# Revit family: Flachrundschraube mit Kombimutter
name_source: partatom
category: Generic Models
revit_build: Autodesk Revit 2015 (Build: 20140606_1530(x64)
units: mm (PartAtom-declared; Revit-internal decimal feet)

## types (14) — shared parameters
Manufacturer = OBO Bettermann
URL = http://www.obo-bettermann.com

## per-type parameters (varying)
| type | GTIN | Length | Length 1 | Manufacturer Art.No. | Material |
| FRSB 6x12 VZ G | 4012195059561 | 12 mm  [stored 0.0393701 ft] | 11 mm  [stored 0.0360892 ft] | 6406133 | Electrogalvanised |
| FRSB 6x12 G | 4012196563111 | 12 mm  [stored 0.0393701 ft] | 11 mm  [stored 0.0360892 ft] | 6406130 | Electrogalvanised |
| FRSB 6x20 G | 4012196616152 | 20 mm  [stored 0.0656168 ft] | 19 mm  [stored 0.062336 ft] | 6406181 | Electrogalvanised |
| FRSB 6x12 VZ F | 4012195059585 | 12 mm  [stored 0.0393701 ft] | 11 mm  [stored 0.0360892 ft] | 6406125 | Hot-dip galvanised |
| FRSB 6x12 F | 4012196199815 | 12 mm  [stored 0.0393701 ft] | 11 mm  [stored 0.0360892 ft] | 6406122 | Hot-dip galvanised |
| FRSB 6x15 F | 4012196199877 | 15 mm  [stored 0.0492126 ft] | 14 mm  [stored 0.0459318 ft] | 6406157 | Hot-dip galvanised |
| FRSB 6x20 F | 4012196199990 | 20 mm  [stored 0.0656168 ft] | 19 mm  [stored 0.062336 ft] | 6406203 | Hot-dip galvanised |
| FRSB 6x30 F | 4012195045243 | 30 mm  [stored 0.0984252 ft] | 29 mm  [stored 0.0951444 ft] | 6406907 | Hot-dip galvanised |
| FRSB 6x12 A2 | 4012196077595 | 12 mm  [stored 0.0393701 ft] | 11 mm  [stored 0.0360892 ft] | 6406138 | Stainless Steel, A2 |
| FRSB 6x16 A2 | 4012196077717 | 16 mm  [stored 0.0524934 ft] | 15 mm  [stored 0.0492126 ft] | 6406189 | Stainless Steel, A2 |
| FRSB 6x20 A2 | 4012195925248 | 20 mm  [stored 0.0656168 ft] | 19 mm  [stored 0.062336 ft] | 6406205 | Stainless Steel, A2 |
| FRSB 6x12 A4 | 4012196078370 | 12 mm  [stored 0.0393701 ft] | 11 mm  [stored 0.0360892 ft] | 6406142 | Stainless Steel, A4 |
| FRSB 6x16 A4 | 4012196078431 | 16 mm  [stored 0.0524934 ft] | 15 mm  [stored 0.0492126 ft] | 6406193 | Stainless Steel, A4 |
| FRSB 6x20 A4 | 4012195925255 | 20 mm  [stored 0.0656168 ft] | 19 mm  [stored 0.062336 ft] | 6406207 | Stainless Steel, A4 |

note: column(s) folded — value = type name in every type: Article Type

note: [stored X ft] marks values corroborated as IEEE doubles in the binary element streams (Revit-internal decimal feet)

## geometry (parser evidence)
native form markers: Sweep x2
no freeform markers — native parametric forms only
